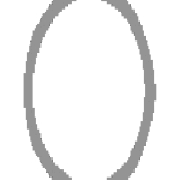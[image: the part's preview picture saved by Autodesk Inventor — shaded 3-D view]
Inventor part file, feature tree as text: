
AUTODESK INVENTOR PART (.ipt)
format: ipt  version: 2021 (Build 250183000, 183)  size: 121,856 bytes
history: native  units: in
note: dims shown in document units (in); Inventor stores cm internally (conversion verified against a paired STEP export)
features: other x4, plane x3, sketch x3, split x2
ambient origin geometry x8: Origin, YZ Plane, XZ Plane, XY Plane, X Axis, Y Axis, Z Axis, Center Point
bodies: Solid1 (feature_tree), Body (feature_tree)
feature tree (12):
  other  "Driven Length"
  other  "Frame Generator"
  other  "Start Plane"
  other  "End Plane"
  plane  "Work Plane5"
  split  "Split1"
  plane  "Work Plane6"
  split  "Split2"
  sketch  "Sketch"  dims[d2=15.2522in d4=-0.0in d5=15.6058in d6=0.12in d7=0.0in d10=90.0deg d9=15.6058in]
  sketch  "Sketch4"  dims[d0=1.0in]
  plane  "Work Plane4"
  sketch  "Sketch5"  dims[d1=0.065in]
